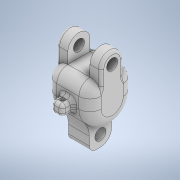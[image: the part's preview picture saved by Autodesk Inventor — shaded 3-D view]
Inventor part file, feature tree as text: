
AUTODESK INVENTOR PART (.ipt)
format: ipt  version: 2022 (Build 260153000, 153)  size: 422,912 bytes
history: native  units: mm
features: fillet x11, extrude x7, sketch x7, other x1
ambient origin geometry x8: Origin, YZ Plane, XZ Plane, XY Plane, X Axis, Y Axis, Z Axis, Center Point
bodies: Solide1 (feature_tree)
feature tree (26):
  other  "Phalange.ipt"
  extrude  "Extrusion1"  Depth=20.0mm
  extrude  "Extrusion2"  Depth=20.0mm
  extrude  "Extrusion3"  Depth=20.0mm TaperAngle=0.0deg
  fillet  "Congé1"  Radius=10.0mm
  fillet  "Congé2"  Radius=10.0mm
  extrude  "Extrusion4"  Depth=20.0mm TaperAngle=0.0deg
  extrude  "Extrusion5"  Depth=5.0mm
  fillet  "Congé4"  Radius=20.0mm
  fillet  "Congé5"  Radius=5.0mm
  fillet  "Congé6"  Radius=10.0mm
  fillet  "Congé7"  Radius=20.0mm
  fillet  "Congé8"  Radius=10.0mm
  fillet  "Congé9"  [1 undecoded]
  fillet  "Congé10"  Radius=10.0mm
  extrude  "Extrusion6"  Depth=5.0mm
  extrude  "Extrusion7"  Depth=43.5mm TaperAngle=0.0deg
  fillet  "Congé11"  Radius=10.0mm
  fillet  "Congé12"  Radius=5.0mm
  sketch  "Esquisse1"
  sketch  "Esquisse3"
  sketch  "Esquisse4"
  sketch  "Esquisse7"
  sketch  "Esquisse8"
  sketch  "Esquisse10"
  sketch  "Esquisse11"
note: 1 required parameter value undecoded (feature->parameter linkage not recoverable at this tier; creation-order binding heuristic only, values carry confidence <= 0.55)
